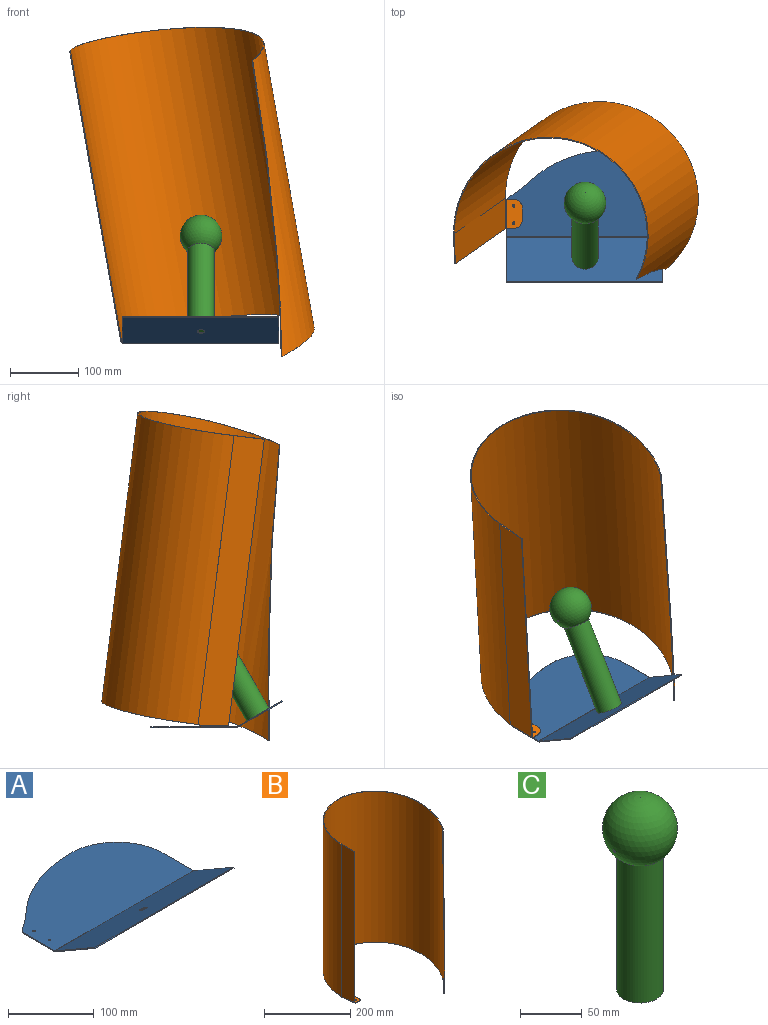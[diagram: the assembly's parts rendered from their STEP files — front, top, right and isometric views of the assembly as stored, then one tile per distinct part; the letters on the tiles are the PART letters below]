
ASSEMBLY  parts=3 mates=3
PART A: 20 faces, bbox 228.6x193x39.2 mm
  f0: cylinder r=177.82mm len=123.17mm, axis (0,0,1), area 165.9mm2, adj f1,f7,f8,f9
  f1: cylinder r=127mm len=24.47mm, axis (0,0,1), area 37.4mm2, adj f0,f2,f8,f9
  f2: cylinder r=9.53mm len=8.25mm, axis (0,0,1), area 12.2mm2, adj f1,f3,f8,f9
  f3: plane 50.15x1.22mm, normal (-1,0,0), area 61.1mm2, adj f2,f8,f9,f17
  f4: plane 50.15x1.22mm, normal (1,0,0), area 61.1mm2, adj f7,f8,f9,f16
  f5: cylinder r=1.44mm len=2.87mm, axis (0,0,1), area 11mm2, adj f8,f9
  f6: cylinder r=1.44mm len=2.87mm, axis (0,0,1), area 11mm2, adj f8,f9
  f7: cylinder r=76.2mm len=76.2mm, axis (0,0,1), area 145.9mm2, adj f0,f4,f8,f9
  f8: plane 228.6x126.35mm, normal (0,0,1), area 23926.1mm2, adj f0,f1,f2,f3,f4,f5,f6,f7
  f9: plane 228.6x126.35mm, normal (0,0,-1), area 23926.1mm2, adj f0,f1,f2,f3,f4,f5,f6,f7
  f10: plane 66.04x38.83mm, normal (-1,0,0), area 92.1mm2, adj f11,f14,f15,f17
  f11: plane 228.6x1.06mm, normal (0,-0.87,0.5), area 278.7mm2, adj f10,f12,f14,f15
  f12: plane 66.04x38.83mm, normal (1,0,0), area 92.1mm2, adj f11,f14,f15,f16
  f13: cylinder r=5.33mm len=10.67mm, axis (0,0.5,0.87), area 40.9mm2, adj f14,f15
  f14: plane 228.6x65.43mm, normal (0,0.5,0.87), area 17180.6mm2, adj f10,f11,f12,f13,f19
  f15: plane 228.6x65.43mm, normal (0,-0.5,-0.87), area 17180.6mm2, adj f10,f11,f12,f13,f18
  f16: plane 1.38x1.22mm, normal (1,0,0), area 1.2mm2, adj f4,f12,f18,f19
  f17: plane 1.38x1.22mm, normal (-1,0,0), area 1.2mm2, adj f3,f10,f18,f19
  f18: cylinder r=2.44mm len=228.6mm, axis (1,0,0), area 291.9mm2, adj f9,f15,f16,f17
  f19: cylinder r=1.22mm len=228.6mm, axis (1,0,0), area 145.9mm2, adj f8,f14,f16,f17
PART B: 26 faces, bbox 282x252.1x482.6 mm
  f0: bspline ~281.95x252.09mm, area 695.7mm2, adj f1,f4,f5,f6
  f1: plane 1.22x0.51mm, normal (0,0,-1), area 0.6mm2, adj f0,f5,f6,f11
  f2: plane 1.22x0.51mm, normal (0,0,1), area 0.6mm2, adj f3,f5,f6,f10
  f3: bspline ~281.92x214.6mm, area 634.8mm2, adj f2,f4,f5,f6
  f4: bspline ~431.8x38.09mm, area 530.8mm2, adj f0,f3,f5,f6
  f5: cylinder r=140.92mm len=482.6mm, axis (0,0,1), area 230812.2mm2, adj f0,f1,f2,f3,f4,f12
  f6: cylinder r=139.7mm len=482.6mm, axis (0,0,1), area 228815.3mm2, adj f0,f1,f2,f3,f4,f8
  f7: cylinder r=1.27mm len=1.41mm, axis (-1,0,0), area 2.4mm2, adj f8,f11,f12,f23
  f8: plane 432.84x44.45mm, normal (1,0,0), area 19126.8mm2, adj f6,f7,f9,f10,f11,f25
  f9: plane 427.61x1.22mm, normal (0,-1,0), area 521.3mm2, adj f8,f10,f12,f22
  f10: plane 44.45x1.22mm, normal (0,0,1), area 54.2mm2, adj f2,f8,f9,f12
  f11: plane 1.22x0.5mm, normal (0,-0.12,-0.99), area 0.6mm2, adj f1,f7,f8,f12
  f12: plane 432.84x44.45mm, normal (-1,0,0), area 19126.8mm2, adj f5,f7,f9,f10,f11,f24
  f13: plane 17.34x3.3mm, normal (0.98,-0.02,-0.17), area 21.1mm2, adj f18,f19,f20,f21
  f14: plane 10.7x3.03mm, normal (0,-0.99,0.12), area 13mm2, adj f18,f19,f20,f22
  f15: cylinder r=1.84mm len=3.84mm, axis (-0.17,-0.12,-0.98), area 14.1mm2, adj f18,f19
  f16: cylinder r=1.84mm len=3.84mm, axis (-0.17,-0.12,-0.98), area 14.1mm2, adj f18,f19
  f17: plane 10.7x3.03mm, normal (0,0.99,-0.12), area 13mm2, adj f18,f19,f21,f23
  f18: plane 42.64x23mm, normal (-0.17,-0.12,-0.98), area 907.3mm2, adj f13,f14,f15,f16,f17,f20,f21,f24
  f19: plane 42.64x23mm, normal (0.17,0.12,0.98), area 907.3mm2, adj f13,f14,f15,f16,f17,f20,f21,f25
  f20: cylinder r=12.7mm len=12.72mm, axis (-0.17,-0.12,-0.98), area 24.3mm2, adj f13,f14,f18,f19
  f21: cylinder r=12.7mm len=13.02mm, axis (-0.17,-0.12,-0.98), area 24.3mm2, adj f13,f17,f18,f19
  f22: bspline ~2.4x2.23mm, area 3.1mm2, adj f9,f14,f24,f25
  f23: plane 2.38x2.23mm, normal (0,0.99,-0.12), area 3.1mm2, adj f7,f17,f24,f25
  f24: cylinder r=2.44mm len=42.82mm, axis (0,-0.99,0.12), area 145.7mm2, adj f12,f18,f22,f23
  f25: cylinder r=1.22mm len=42.68mm, axis (0,-0.99,0.12), area 72.8mm2, adj f8,f19,f22,f23
PART C: 4 faces, bbox 61x61x190.5 mm
  f0: sphere r=30.48mm, area 10383.4mm2, adj f2,f3
  f1: plane 38.1x38.1mm, normal (0,0,-1), area 1140.1mm2, adj f2
  f2: cylinder r=19.05mm len=136.23mm, axis (0,0,1), area 16305.6mm2, adj f0,f1
  f3: cylinder r=1.27mm len=59.62mm, axis (-1,0,0), area 470.5mm2, adj f0
PLACE A at identity fixed
PLACE B rot(axis=(0.57,-0.82,0.05),12.2deg) t=(136.43,6.22,28.95)mm
PLACE C rot(axis=(-1,0,0),30deg) t=(115.06,-81.11,18.91)mm
MATE revolute A.f5 <-> B.f16  axis (0,0,1) through (10.92,-30.48,1.22)mm
MATE revolute B.f15 <-> A.f6  axis (0,0,-1) through (10.92,-5.08,1.22)mm
MATE revolute C.f2 <-> A.f13  axis (0,-0.5,-0.87) through (115.06,-81.11,18.91)mm
